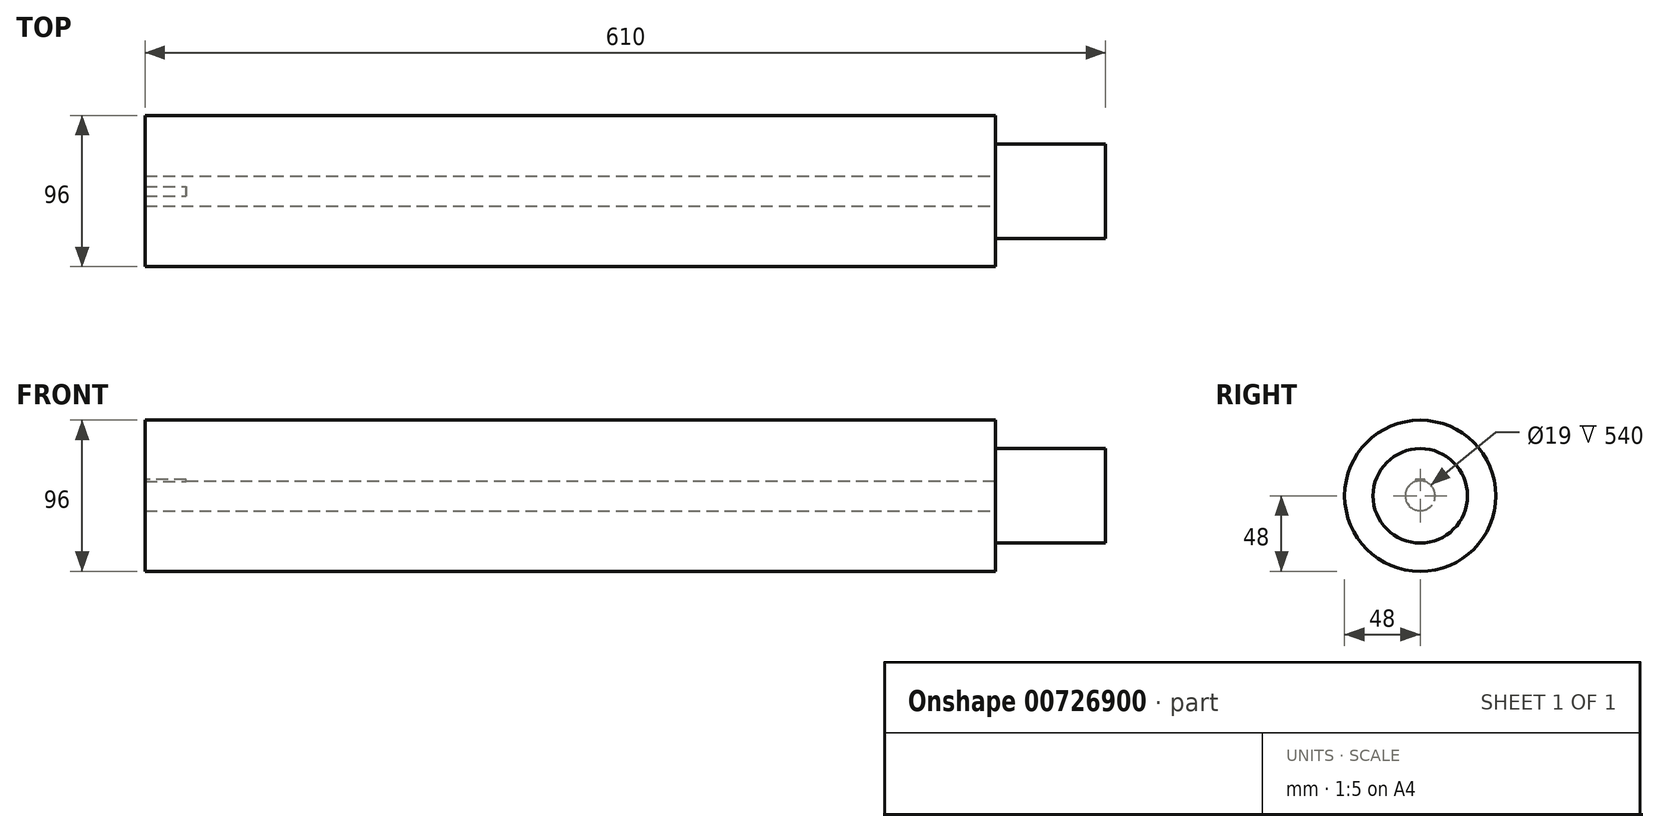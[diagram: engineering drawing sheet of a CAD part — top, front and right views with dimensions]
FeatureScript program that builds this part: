
annotation { "Feature Type Name" : "Feature", "Feature Type Description" : "" }
export const myFeature = defineFeature(function(context is Context, id is Id, definition is map)
    precondition{}
    {
        {
            var Q0;
            Q0=qCreatedBy(makeId("Front.planeOp"),FACE);
            var sketch = newSketch(context, id + "F0", { "sketchPlane" : qUnion([Q0])});
            skLineSegment(sketch, "E0", {"start": v(0, 0) * mm, "end": v(0, 9.5) * mm});
            skLineSegment(sketch, "E1", {"start": v(0, 9.5) * mm, "end": v(-540, 9.5) * mm});
            skLineSegment(sketch, "E2", {"start": v(0, 9.5) * mm, "end": v(0, 48) * mm});
            skLineSegment(sketch, "E3", {"start": v(0, 48) * mm, "end": v(-540, 48) * mm});
            skLineSegment(sketch, "E4", {"start": v(-540, 48) * mm, "end": v(-540, 9.5) * mm});
            skLineSegment(sketch, "E5", {"start": v(0, 0) * mm, "end": v(0, 30) * mm});
            skLineSegment(sketch, "E6", {"start": v(0, 30) * mm, "end": v(70, 30) * mm});
            skLineSegment(sketch, "E7", {"start": v(70, 30) * mm, "end": v(70, 0) * mm});
            skLineSegment(sketch, "E8", {"start": v(70, 0) * mm, "end": v(0, 0) * mm});
            skSolve(sketch);
        }
        {
            var Q0;
            Q0 = qSketchRegion(id + "F0", true);
            var Q1;
            Q1=sQuery(id+"F0.wireOp",EDGE,"E8");
            revolve(context, id + "F1", {"surfaceOperationType" : NewSurfaceOperationType.NEW, "entities" : qUnion([Q0]), "axis" : qUnion([Q1]), "revolveType" : RevolveType.FULL});
        }
        {
            var Q0;
            Q0=makeQuery(id+"F1.opRevolve","SWEPT_FACE",FACE,{"disambiguationData":[OSD([sQuery(id+"F0.wireOp",EDGE,"E4")])]});
            var sketch = newSketch(context, id + "F2", { "sketchPlane" : qUnion([Q0])});
            skLineSegment(sketch, "E9", {"start": v(0, 8.5) * mm, "end": v(-3, 8.5) * mm});
            skLineSegment(sketch, "E10", {"start": v(-3, 8.5) * mm, "end": v(-3, 10.5) * mm});
            skLineSegment(sketch, "E11", {"start": v(-3, 10.5) * mm, "end": v(3, 10.5) * mm});
            skLineSegment(sketch, "E12", {"start": v(3, 10.5) * mm, "end": v(3, 8.5) * mm});
            skLineSegment(sketch, "E13", {"start": v(3, 8.5) * mm, "end": v(0, 8.5) * mm});
            skSolve(sketch);
        }
        {
            var Q0;
            Q0 = qSketchRegion(id + "F2", true);
            extrude(context, id + "F3", {"entities" : qUnion([Q0]), "operationType" : NewBodyOperationType.REMOVE, "oppositeDirection" : true, "depth" : 26 * mm, "offsetDistance" : 25 * mm});
        }
    });
